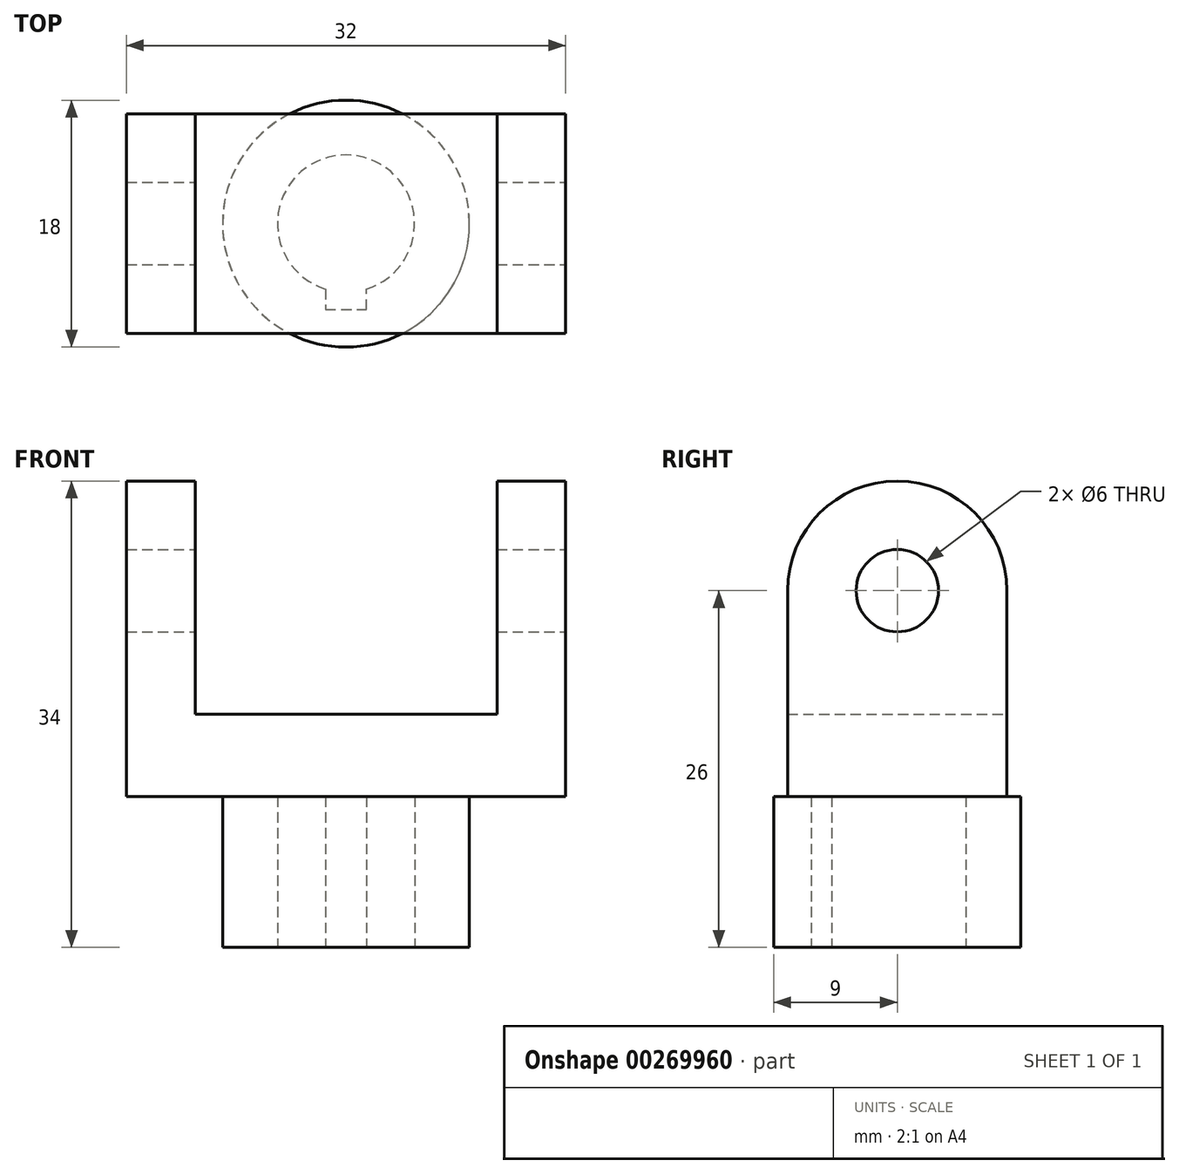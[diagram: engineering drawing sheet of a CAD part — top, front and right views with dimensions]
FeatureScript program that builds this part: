
annotation { "Feature Type Name" : "Feature", "Feature Type Description" : "" }
export const myFeature = defineFeature(function(context is Context, id is Id, definition is map)
    precondition{}
    {
        {
            var Q0;
            Q0=qCreatedBy(makeId("Front.planeOp"),FACE);
            var sketch = newSketch(context, id + "F0", { "sketchPlane" : qUnion([Q0])});
            skLineSegment(sketch, "E0", {"start": v(0, 0) * mm, "end": v(32, 0) * mm});
            skLineSegment(sketch, "E1", {"start": v(32, 0) * mm, "end": v(32, 23) * mm});
            skLineSegment(sketch, "E2", {"start": v(32, 23) * mm, "end": v(27, 23) * mm});
            skLineSegment(sketch, "E3", {"start": v(27, 23) * mm, "end": v(27, 6) * mm});
            skLineSegment(sketch, "E4", {"start": v(27, 6) * mm, "end": v(5, 6) * mm});
            skLineSegment(sketch, "E5", {"start": v(5, 6) * mm, "end": v(5, 23) * mm});
            skLineSegment(sketch, "E6", {"start": v(5, 23) * mm, "end": v(0, 23) * mm});
            skLineSegment(sketch, "E7", {"start": v(0, 23) * mm, "end": v(0, 0) * mm});
            skLineSegment(sketch, "E8", {"start": v(16, 0) * mm, "end": v(16, -11) * mm});
            skLineSegment(sketch, "E9", {"start": v(16, -11) * mm, "end": v(7, -11) * mm});
            skLineSegment(sketch, "E10", {"start": v(7, -11) * mm, "end": v(7, 0) * mm});
            skSolve(sketch);
        }
        {
            var Q0;
            {var subQ0=sQuery(id+"F0.wireOp",EDGE,"E8");Q0=makeQuery(id+"F0.imprint","IMPRINT",FACE,{"disambiguationData":[TD([[makeQuery(id+"F0.imprint","IMPRINT",EDGE,{"derivedFrom":subQ0}),-1.0]])]});}
            var Q1;
            Q1=sQuery(id+"F0.wireOp",EDGE,"E8");
            revolve(context, id + "F1", {"entities" : qUnion([Q0]), "axis" : qUnion([Q1]), "revolveType" : RevolveType.FULL});
        }
        {
            var Q0;
            Q0=qSketchRegion(id+"FJ9KJaCrt9Enqb2_0",true);
            var Q1;
            {var subQ0=sQuery(id+"F0.wireOp",EDGE,"E1");Q1=makeQuery(id+"F0.imprint","IMPRINT",FACE,{"disambiguationData":[TD([[makeQuery(id+"F0.imprint","IMPRINT",EDGE,{"derivedFrom":subQ0}),1.0]])]});}
            extrude(context, id + "F2", {"entities" : qUnion([Q0, Q1]), "operationType" : NewBodyOperationType.ADD, "endBound" : BoundingType.SYMMETRIC, "depth" : 16 * mm});
        }
        {
            var Q0;
            Q0=makeQuery(id+"F1.opRevolve","SWEPT_FACE",FACE,{"disambiguationData":[OSD([sQuery(id+"F0.wireOp",EDGE,"E9")])]});
            var sketch = newSketch(context, id + "F3", { "sketchPlane" : qUnion([Q0])});
            skArc(sketch, "E11", {"start": v(14.5, 4.77) * mm, "mid": v(16, -5) * mm, "end": v(17.5, 4.77) * mm});
            skLineSegment(sketch, "E12", {"start": v(14.5, 4.77) * mm, "end": v(14.5, 6.27) * mm});
            skLineSegment(sketch, "E13", {"start": v(14.5, 6.27) * mm, "end": v(17.5, 6.27) * mm});
            skLineSegment(sketch, "E14", {"start": v(17.5, 6.27) * mm, "end": v(17.5, 4.77) * mm});
            skLineSegment(sketch, "E15", {"start": v(16, 6.27) * mm, "end": v(16, 15.34) * mm, "construction": true});
            skSolve(sketch);
        }
        {
            var Q0;
            Q0=makeQuery(id+"F3.imprint","IMPRINT",FACE,{"disambiguationData":[TD([[makeQuery(id+"F3.imprint","IMPRINT",EDGE,{"derivedFrom":sQuery(id+"F3.wireOp",EDGE,"E11")}),1.0]])]});
            extrude(context, id + "F4", {"entities" : qUnion([Q0]), "operationType" : NewBodyOperationType.REMOVE, "oppositeDirection" : true, "depth" : 11 * mm});
        }
        {
            var Q0;
            Q0=makeQuery(id+"F2.opExtrude","SWEPT_FACE",FACE,{"disambiguationData":[OSD([sQuery(id+"F0.wireOp",EDGE,"E1")])]});
            var sketch = newSketch(context, id + "F5", { "sketchPlane" : qUnion([Q0])});
            skCircle(sketch, "E16", {"center": v(0, 15) * mm, "radius": 3 * mm});
            skArc(sketch, "E17", {"start": v(8, 15) * mm, "mid": v(0, 23) * mm, "end": v(-8, 15) * mm});
            skLineSegment(sketch, "E18.0", {"start": v(-8, 15) * mm, "end": v(-8, 23) * mm});
            skLineSegment(sketch, "E19.0", {"start": v(-8, 23) * mm, "end": v(8, 23) * mm});
            skLineSegment(sketch, "E20.0", {"start": v(8, 0) * mm, "end": v(8, 23) * mm});
            skPoint(sketch, "E21.orphan", {"position": v(-8, 0) * mm});
            skSolve(sketch);
        }
        {
            var Q0;
            Q0=qSketchRegion(id+"F5",true);
            extrude(context, id + "F6", {"entities" : qUnion([Q0]), "operationType" : NewBodyOperationType.REMOVE, "endBound" : BoundingType.THROUGH_ALL, "oppositeDirection" : true, "depth" : 25 * mm});
        }
    });
